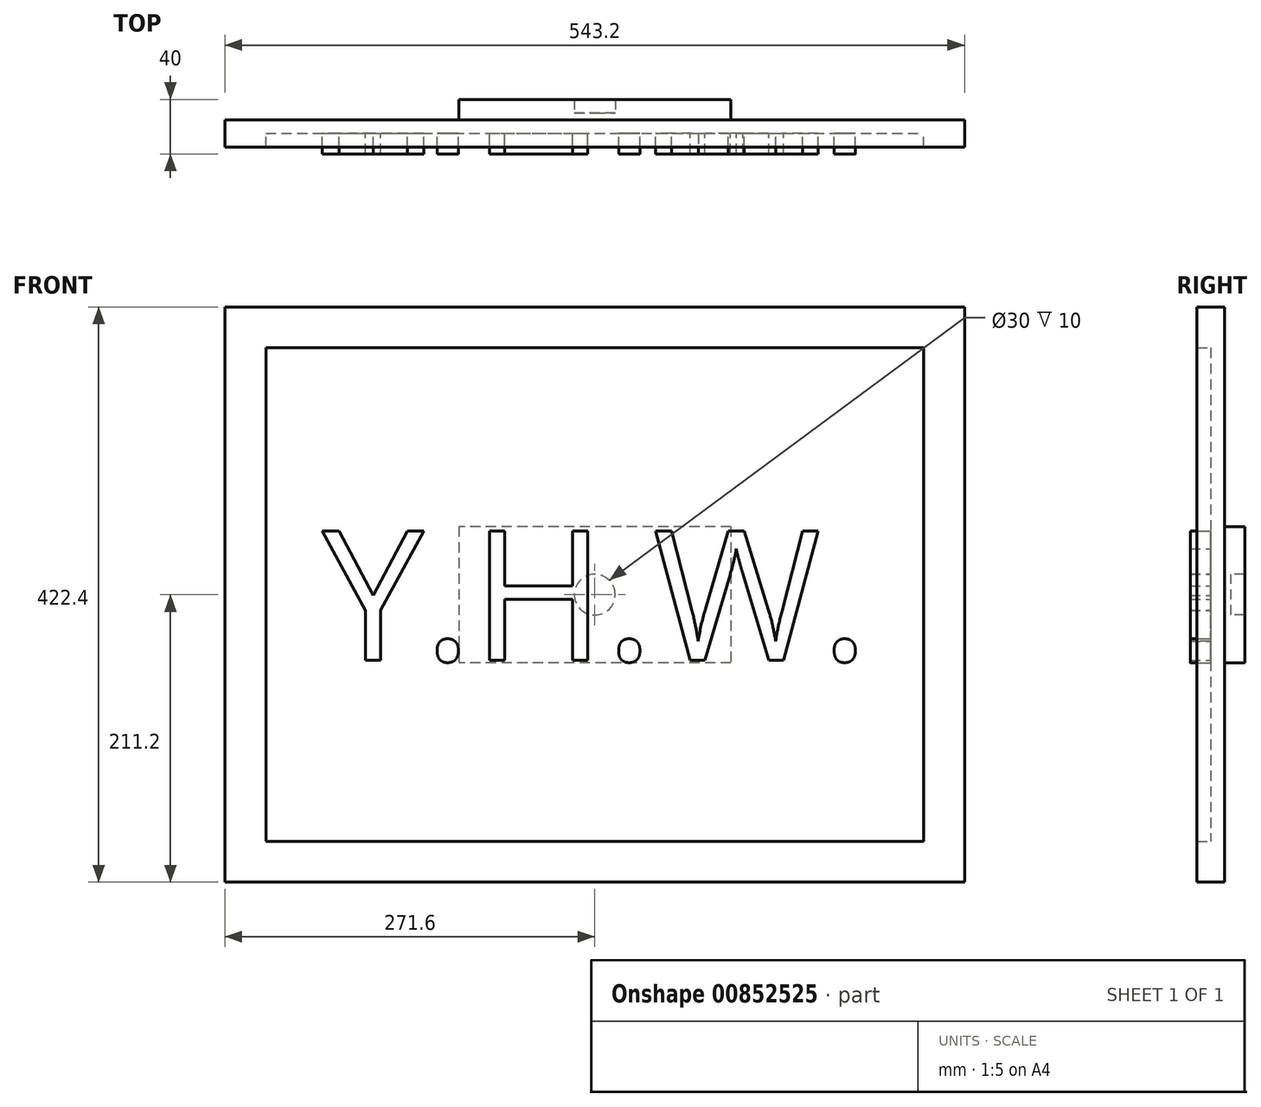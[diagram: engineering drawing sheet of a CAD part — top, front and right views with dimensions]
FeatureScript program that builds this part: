
annotation { "Feature Type Name" : "Feature", "Feature Type Description" : "" }
export const myFeature = defineFeature(function(context is Context, id is Id, definition is map)
    precondition{}
    {
        {
            var Q0;
            Q0=qCreatedBy(makeId("Front.planeOp"),FACE);
            var sketch = newSketch(context, id + "F0", { "sketchPlane" : qUnion([Q0])});
            skLineSegment(sketch, "E0.bottom", {"start": v(-241.6, 181.2) * mm, "end": v(241.6, 181.2) * mm});
            skLineSegment(sketch, "E0.top", {"start": v(-241.6, -181.2) * mm, "end": v(241.6, -181.2) * mm});
            skLineSegment(sketch, "E0.left", {"start": v(-241.6, 181.2) * mm, "end": v(-241.6, -181.2) * mm});
            skLineSegment(sketch, "E0.right", {"start": v(241.6, 181.2) * mm, "end": v(241.6, -181.2) * mm});
            skLineSegment(sketch, "E1.0", {"start": v(-271.6, 211.2) * mm, "end": v(271.6, 211.2) * mm});
            skLineSegment(sketch, "E1.1", {"start": v(-271.6, 211.2) * mm, "end": v(-271.6, -211.2) * mm});
            skLineSegment(sketch, "E1.2", {"start": v(-271.6, -211.2) * mm, "end": v(271.6, -211.2) * mm});
            skLineSegment(sketch, "E1.3", {"start": v(271.6, 211.2) * mm, "end": v(271.6, -211.2) * mm});
            skSolve(sketch);
        }
        {
            var Q0;
            Q0=makeQuery(id+"F0.imprint","IMPRINT",FACE,{"disambiguationData":[TD([[makeQuery(id+"F0.imprint","IMPRINT",EDGE,{"derivedFrom":sQuery(id+"F0.wireOp",EDGE,"E0.bottom")}),1.0]])]});
            extrude(context, id + "F1", {"entities" : qUnion([Q0]), "depth" : 20 * mm, "offsetDistance" : 25 * mm});
        }
        {
            var Q0;
            Q0=makeQuery(id+"F0.imprint","IMPRINT",FACE,{"disambiguationData":[TD([[makeQuery(id+"F0.imprint","IMPRINT",EDGE,{"derivedFrom":sQuery(id+"F0.wireOp",EDGE,"E0.bottom")}),-1.0]])]});
            extrude(context, id + "F2", {"entities" : qUnion([Q0]), "operationType" : NewBodyOperationType.ADD, "depth" : 10 * mm, "offsetDistance" : 25 * mm});
        }
        {
            var Q0;
            Q0=makeQuery(id+"F0.imprint","IMPRINT",FACE,{"disambiguationData":[TD([[makeQuery(id+"F0.imprint","IMPRINT",EDGE,{"derivedFrom":sQuery(id+"F0.wireOp",EDGE,"E0.bottom")}),-1.0]])]});
            var sketch = newSketch(context, id + "F3", { "sketchPlane" : qUnion([Q0])});
            skLineSegment(sketch, "E2.bottom", {"start": v(100, 50) * mm, "end": v(-100, 50) * mm});
            skLineSegment(sketch, "E2.top", {"start": v(100, -50) * mm, "end": v(-100, -50) * mm});
            skLineSegment(sketch, "E2.left", {"start": v(100, 50) * mm, "end": v(100, -50) * mm});
            skLineSegment(sketch, "E2.right", {"start": v(-100, 50) * mm, "end": v(-100, -50) * mm});
            skCircle(sketch, "E3", {"center": v(0, 0) * mm, "radius": 15 * mm});
            skSolve(sketch);
        }
        {
            var Q0;
            Q0=makeQuery(id+"F3.imprint","IMPRINT",FACE,{"disambiguationData":[TD([[makeQuery(id+"F3.imprint","IMPRINT",EDGE,{"derivedFrom":sQuery(id+"F3.wireOp",EDGE,"E2.bottom")}),1.0]])]});
            extrude(context, id + "F4", {"entities" : qUnion([Q0]), "operationType" : NewBodyOperationType.ADD, "oppositeDirection" : true, "depth" : 15 * mm, "offsetDistance" : 25 * mm});
        }
        {
            var Q0;
            Q0=makeQuery(id+"F3.imprint","IMPRINT",FACE,{"disambiguationData":[TD([[makeQuery(id+"F3.imprint","IMPRINT",EDGE,{"derivedFrom":sQuery(id+"F3.wireOp",EDGE,"E3")}),1.0]])]});
            extrude(context, id + "F5", {"entities" : qUnion([Q0]), "operationType" : NewBodyOperationType.ADD, "oppositeDirection" : true, "depth" : 5 * mm, "offsetDistance" : 25 * mm});
        }
        {
            var Q0;
            Q0=qCreatedBy(makeId("Front.planeOp"),FACE);
            var sketch = newSketch(context, id + "F6", { "sketchPlane" : qUnion([Q0])});
            skText(sketch, "E4", { "text": "Y.H.W.", "fontName": "OpenSans-Regular.ttf"});
            const initialGuessF6  = {"E4": [-0.2, -0.04808, 1, 0, 0.0956]};
            skSetInitialGuess(sketch, initialGuessF6);
            skSolve(sketch);
        }
        {
            var Q0;
            Q0 = qSketchRegion(id + "F6", true);
            extrude(context, id + "F7", {"entities" : qUnion([Q0]), "operationType" : NewBodyOperationType.ADD, "depth" : 25 * mm, "offsetDistance" : 25 * mm});
        }
    });
